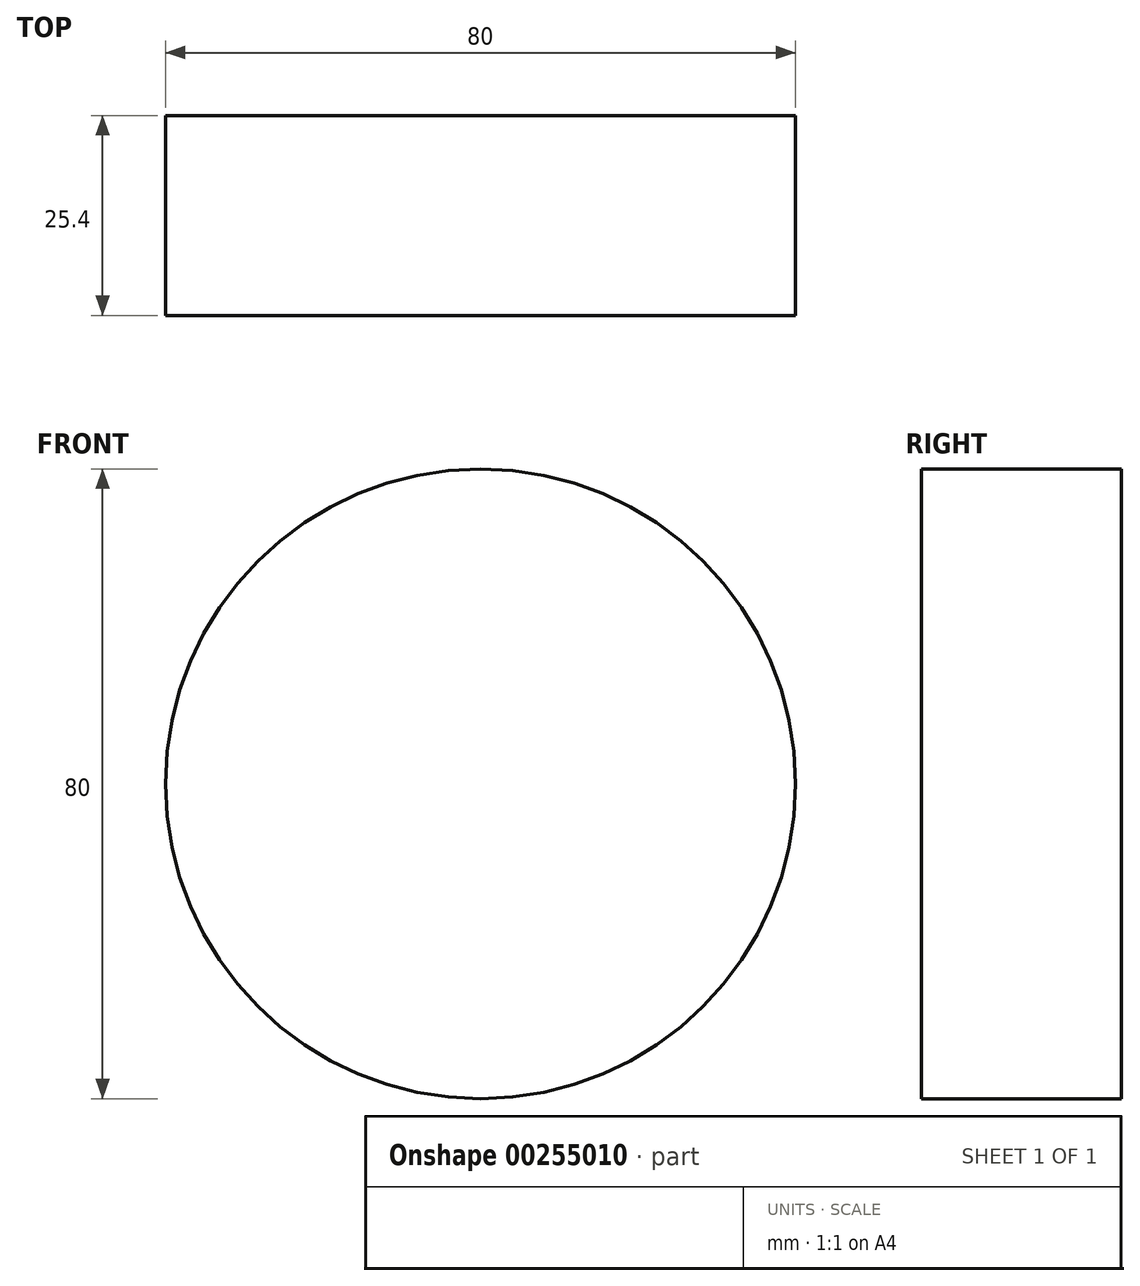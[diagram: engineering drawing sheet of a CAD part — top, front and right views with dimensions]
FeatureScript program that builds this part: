
annotation { "Feature Type Name" : "Feature", "Feature Type Description" : "" }
export const myFeature = defineFeature(function(context is Context, id is Id, definition is map)
    precondition{}
    {
        {
            var Q0;
            Q0=qCreatedBy(makeId("Front.planeOp"),FACE);
            var sketch = newSketch(context, id + "F0", { "sketchPlane" : qUnion([Q0])});
            skCircle(sketch, "E0", {"center": v(0, 0) * mm, "radius": 40 * mm});
            skSolve(sketch);
        }
        {
            var Q0;
            Q0 = qSketchRegion(id + "F0", true);
            extrude(context, id + "F1", {"entities" : qUnion([Q0]), "depth" : 25.4 * mm});
        }
    });
